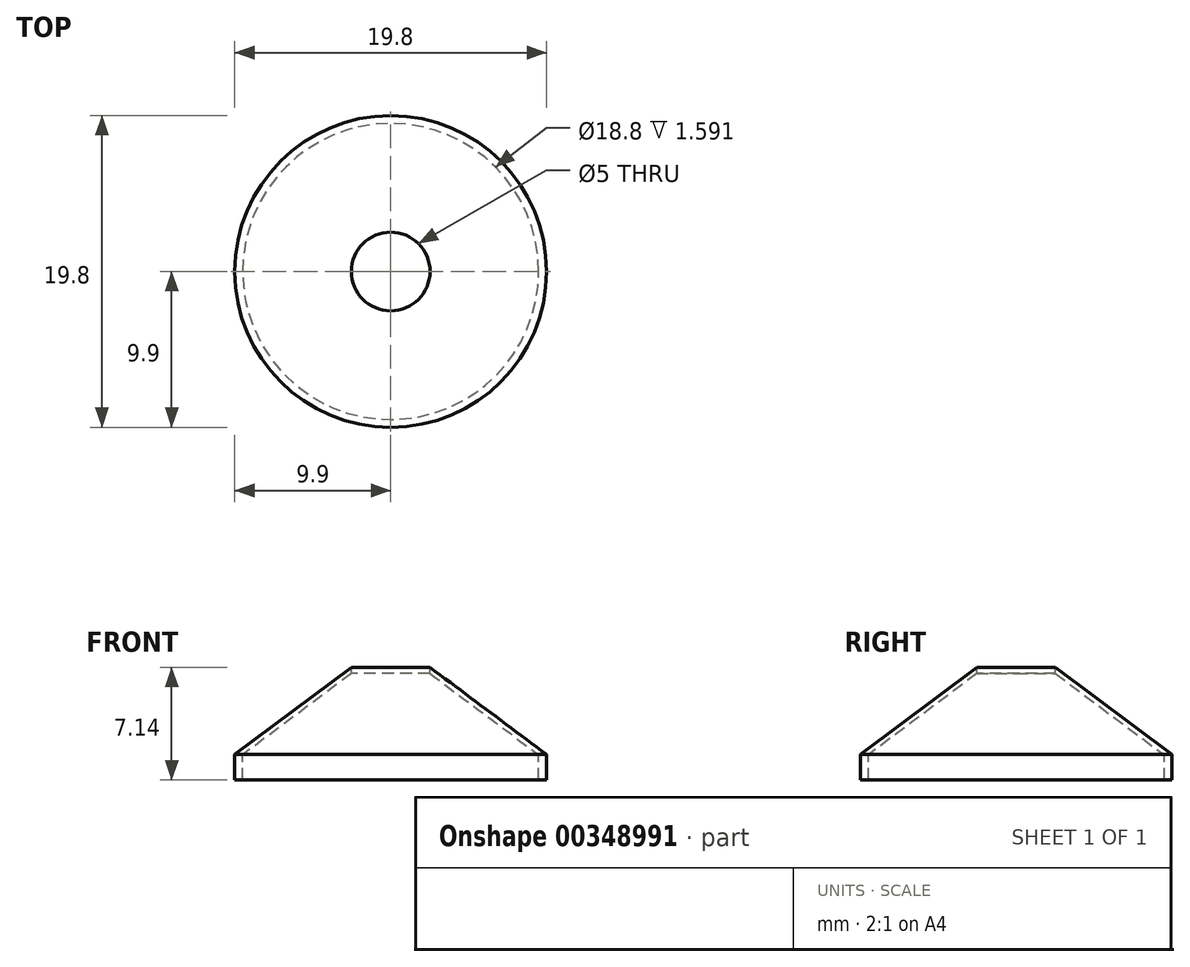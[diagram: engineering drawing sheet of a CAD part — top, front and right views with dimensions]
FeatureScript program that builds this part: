
annotation { "Feature Type Name" : "Feature", "Feature Type Description" : "" }
export const myFeature = defineFeature(function(context is Context, id is Id, definition is map)
    precondition{}
    {
        {
            var Q0;
            Q0=qCreatedBy(makeId("Front.planeOp"),FACE);
            var sketch = newSketch(context, id + "F0", { "sketchPlane" : qUnion([Q0])});
            skLineSegment(sketch, "E0", {"start": v(0, 0) * mm, "end": v(-9.9, 0) * mm});
            skLineSegment(sketch, "E1", {"start": v(-9.9, 0) * mm, "end": v(-9.9, 1.6) * mm});
            skLineSegment(sketch, "E2", {"start": v(-9.9, 1.6) * mm, "end": v(-2.5, 7.14) * mm});
            skLineSegment(sketch, "E3", {"start": v(-2.5, 7.14) * mm, "end": v(-2.5, 9.25) * mm});
            skLineSegment(sketch, "E4", {"start": v(0, 9.5) * mm, "end": v(0, 0) * mm});
            skLineSegment(sketch, "E5", {"start": v(-9.4, 0) * mm, "end": v(-9.4, 1.6) * mm});
            skLineSegment(sketch, "E6", {"start": v(-9.4, 1.6) * mm, "end": v(-2.5, 6.75) * mm});
            skLineSegment(sketch, "E7", {"start": v(-2.5, 6.75) * mm, "end": v(-2.5, 7.14) * mm});
            skPoint(sketch, "E8", {"position": v(0, 0) * mm});
            skPoint(sketch, "E9", {"position": v(-19.07, -4.84) * mm});
            skSolve(sketch);
        }
        {
            var Q0;
            Q0 = qSketchRegion(id + "F0", true);
            var Q1;
            Q1=sQuery(id+"F0.wireOp",EDGE,"E4");
            revolve(context, id + "F1", {"entities" : qUnion([Q0]), "axis" : qUnion([Q1]), "revolveType" : RevolveType.FULL});
        }
    });
